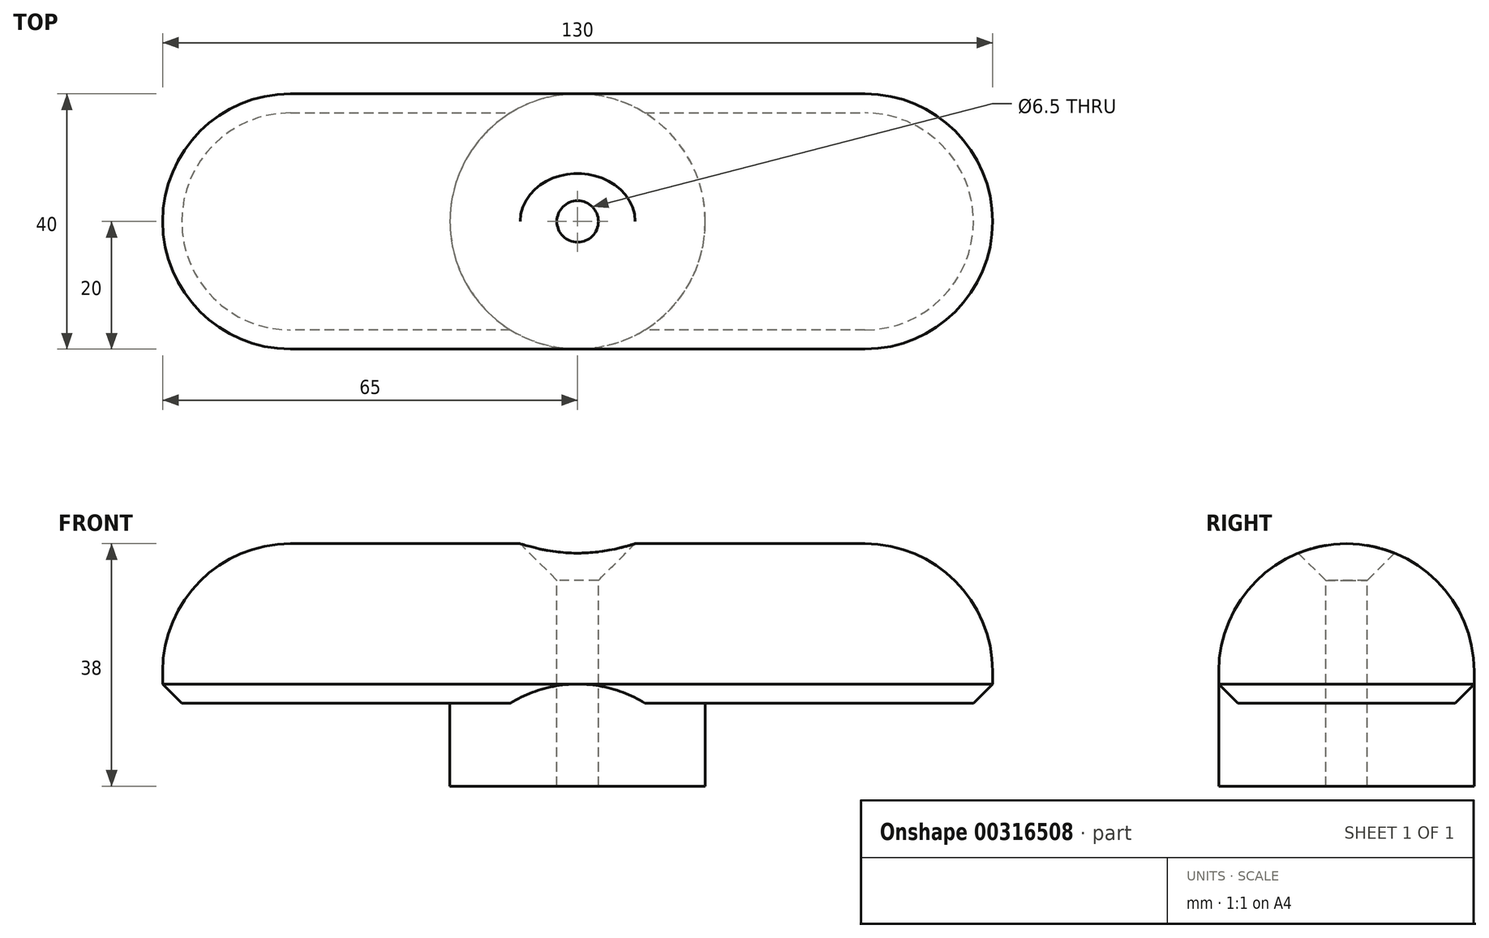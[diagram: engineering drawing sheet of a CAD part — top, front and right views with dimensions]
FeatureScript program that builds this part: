
annotation { "Feature Type Name" : "Feature", "Feature Type Description" : "" }
export const myFeature = defineFeature(function(context is Context, id is Id, definition is map)
    precondition{}
    {
        {
            var Q0;
            Q0=qCreatedBy(makeId("Top.planeOp"),FACE);
            var sketch = newSketch(context, id + "F0", { "sketchPlane" : qUnion([Q0])});
            skLineSegment(sketch, "E0.bottom", {"start": v(-45, -20) * mm, "end": v(45, -20) * mm});
            skLineSegment(sketch, "E0.top", {"start": v(-45, 20) * mm, "end": v(45, 20) * mm});
            skLineSegment(sketch, "E0.left", {"start": v(-65, 0) * mm, "end": v(-65, 0) * mm});
            skLineSegment(sketch, "E0.right", {"start": v(65, 0) * mm, "end": v(65, 0) * mm});
            skPoint(sketch, "E0.middle", {"position": v(0, 0) * mm});
            skCircle(sketch, "E1", {"center": v(0, 0) * mm, "radius": 20 * mm});
            skPoint(sketch, "E2.visualSharp", {"position": v(-65, 20) * mm});
            skArc(sketch, "E2.filletArc", {"start": v(-45, 20) * mm, "mid": v(-59.14, 14.14) * mm, "end": v(-65, 0) * mm});
            skPoint(sketch, "E3.visualSharp", {"position": v(-65, -20) * mm});
            skArc(sketch, "E3.filletArc", {"start": v(-65, 0) * mm, "mid": v(-59.14, -14.14) * mm, "end": v(-45, -20) * mm});
            skPoint(sketch, "E4.visualSharp", {"position": v(65, -20) * mm});
            skArc(sketch, "E4.filletArc", {"start": v(45, -20) * mm, "mid": v(59.14, -14.14) * mm, "end": v(65, 0) * mm});
            skPoint(sketch, "E5.visualSharp", {"position": v(65, 20) * mm});
            skArc(sketch, "E5.filletArc", {"start": v(65, 0) * mm, "mid": v(59.14, 14.14) * mm, "end": v(45, 20) * mm});
            skSolve(sketch);
        }
        {
            var Q0;
            Q0 = qSketchRegion(id + "F0", true);
            extrude(context, id + "F1", {"entities" : qUnion([Q0]), "oppositeDirection" : true, "depth" : 25 * mm});
        }
        {
            var Q0;
            {var subQ0=sQuery(id+"F0.wireOp",EDGE,"E1");var subQ1=makeQuery(id+"F0.imprint","INTERSECT",VERTEX,{"derivedFrom":[sQuery(id+"F0.wireOp",EDGE,"E0.bottom"),subQ0]});Q0=makeQuery(id+"F0.imprint","IMPRINT",FACE,{"disambiguationData":[TD([[makeQuery(id+"F0.imprint","IMPRINT",EDGE,{"disambiguationData":[TD([[subQ1,1.0]])],"derivedFrom":subQ0}),1.0]])]});}
            extrude(context, id + "F2", {"entities" : qUnion([Q0]), "operationType" : NewBodyOperationType.ADD, "oppositeDirection" : true, "depth" : 38 * mm});
        }
        {
            var Q0;
            Q0=sQuery(id+"F0.wireOp",VERTEX,"E0.middle");
            var Q1;
            Q1=makeQuery(id+"F1.opExtrude","SWEPT_BODY",BODY,{"disambiguationData":[OSD([sQuery(id+"F0.wireOp",EDGE,"E0.bottom"),sQuery(id+"F0.wireOp",EDGE,"E0.top"),sQuery(id+"F0.wireOp",EDGE,"E2.filletArc"),sQuery(id+"F0.wireOp",EDGE,"E3.filletArc"),sQuery(id+"F0.wireOp",EDGE,"E4.filletArc"),sQuery(id+"F0.wireOp",EDGE,"E5.filletArc")])]});
            hole(context, id + "F3", {"style" : HoleStyle.C_SINK, "endStyle" : HoleEndStyle.THROUGH, "holeDiameter" : 6.5 * mm, "cSinkDiameter" : 18 * mm, "cSinkAngle" : 90 * degree, "tappedDepth" : 12 * mm, "tapClearance" : 3, "locations" : qUnion([Q0]), "scope" : qUnion([Q1])});
        }
        {
            var Q0;
            Q0=makeQuery(id+"F1.opExtrude","CAP_EDGE",EDGE,{"disambiguationData":[OSD([sQuery(id+"F0.wireOp",EDGE,"E0.bottom")])],"isStart":true});
            fillet(context, id + "F4", {"entities" : qUnion([Q0]), "radius" : 20 * mm, "tangentPropagation" : true, "allowEdgeOverflow" : false});
        }
        {
            var Q0;
            {var subQ0=sQuery(id+"F0.wireOp",EDGE,"E3.filletArc");var subQ1=sQuery(id+"F0.wireOp",EDGE,"E2.filletArc");var subQ2=sQuery(id+"F0.wireOp",EDGE,"E0.top");Q0=makeQuery(id+"F2.boolean.opBoolean","SPLIT",EDGE,{"disambiguationData":[TD([makeQuery(id+"F1.opExtrude","SWEPT_FACE",FACE,{"disambiguationData":[OSD([subQ1,subQ0])]})])],"derivedFrom":makeQuery(id+"F1.opExtrude","CAP_EDGE",EDGE,{"disambiguationData":[OSD([subQ2])],"isStart":false})});}
            chamfer(context, id + "F5", {"entities" : qUnion([Q0]), "width" : 3 * mm, "tangentPropagation" : true});
        }
    });
